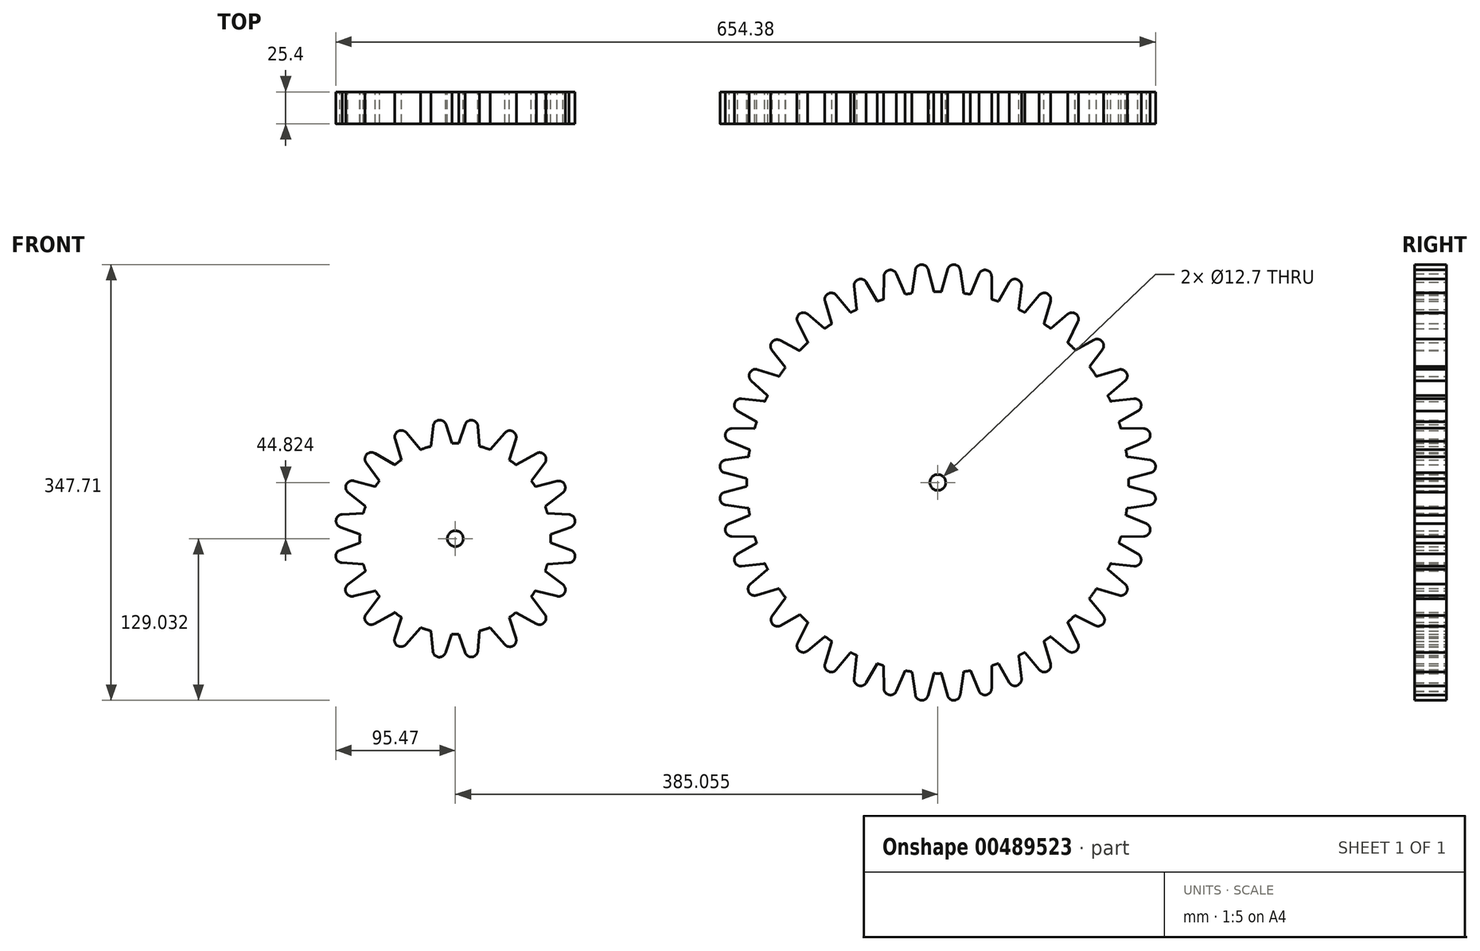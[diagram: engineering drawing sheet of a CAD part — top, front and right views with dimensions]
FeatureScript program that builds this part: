
annotation { "Feature Type Name" : "Feature", "Feature Type Description" : "" }
export const myFeature = defineFeature(function(context is Context, id is Id, definition is map)
    precondition{}
    {
        {
            var Q0;
            Q0=qCreatedBy(makeId("Front.planeOp"),FACE);
            var sketch = newSketch(context, id + "F0", { "sketchPlane" : qUnion([Q0])});
            skCircle(sketch, "E0", {"center": v(90.4, 32.98) * mm, "radius": 152.4 * mm});
            skCircle(sketch, "E1", {"center": v(90.4, 32.98) * mm, "radius": 6.35 * mm});
            skCircle(sketch, "E2", {"center": v(-294.65, -11.85) * mm, "radius": 76.2 * mm});
            skCircle(sketch, "E3", {"center": v(-294.65, -11.85) * mm, "radius": 6.35 * mm});
            skLineSegment(sketch, "E4", {"start": v(-78.98, 50.92) * mm, "end": v(-61.5, 53.51) * mm});
            skLineSegment(sketch, "E5", {"start": v(-57.15, 49.41) * mm, "end": v(-58.01, 39.52) * mm});
            skLineSegment(sketch, "E6", {"start": v(-62.8, 36.17) * mm, "end": v(-79.65, 40.7) * mm});
            skPoint(sketch, "E7.visualSharp", {"position": v(-82.74, 41.52) * mm});
            skPoint(sketch, "E8.visualSharp", {"position": v(-81.95, 50.47) * mm});
            skArc(sketch, "E9.filletArc", {"start": v(-57.15, 49.41) * mm, "mid": v(-58.33, 52.52) * mm, "end": v(-61.5, 53.51) * mm});
            skArc(sketch, "E10.filletArc", {"start": v(-62.8, 36.17) * mm, "mid": v(-59.62, 36.73) * mm, "end": v(-58.01, 39.52) * mm});
            skLineSegment(sketch, "E11", {"start": v(-66.15, 99.78) * mm, "end": v(-48.58, 97.84) * mm});
            skLineSegment(sketch, "E12", {"start": v(-45.42, 92.76) * mm, "end": v(-48.78, 83.42) * mm});
            skLineSegment(sketch, "E13", {"start": v(-54.25, 81.4) * mm, "end": v(-69.4, 90.07) * mm});
            skPoint(sketch, "E14.visualSharp", {"position": v(-72.18, 91.66) * mm});
            skArc(sketch, "E15.filletArc", {"start": v(-45.42, 92.76) * mm, "mid": v(-45.77, 96.07) * mm, "end": v(-48.58, 97.84) * mm});
            skArc(sketch, "E16.filletArc", {"start": v(-54.25, 81.4) * mm, "mid": v(-51.05, 81.13) * mm, "end": v(-48.78, 83.42) * mm});
            skLineSegment(sketch, "E17", {"start": v(-53.37, 123.14) * mm, "end": v(-37.03, 117.86) * mm});
            skLineSegment(sketch, "E18", {"start": v(-34.9, 112.33) * mm, "end": v(-39.88, 103.71) * mm});
            skLineSegment(sketch, "E19", {"start": v(-45.73, 102.79) * mm, "end": v(-58.48, 114.27) * mm});
            skPoint(sketch, "E20.visualSharp", {"position": v(-60.77, 116.34) * mm});
            skPoint(sketch, "E21.visualSharp", {"position": v(-56.3, 124.09) * mm});
            skArc(sketch, "E22.filletArc", {"start": v(-34.9, 112.33) * mm, "mid": v(-34.65, 115.6) * mm, "end": v(-37.03, 117.86) * mm});
            skArc(sketch, "E23.filletArc", {"start": v(-45.73, 102.79) * mm, "mid": v(-42.58, 101.85) * mm, "end": v(-39.88, 103.71) * mm});
            skLineSegment(sketch, "E24", {"start": v(-74.04, 75.96) * mm, "end": v(-56.37, 76.18) * mm});
            skLineSegment(sketch, "E25", {"start": v(-52.61, 71.53) * mm, "end": v(-54.8, 61.85) * mm});
            skLineSegment(sketch, "E26", {"start": v(-59.99, 59.17) * mm, "end": v(-76.08, 65.92) * mm});
            skPoint(sketch, "E27.visualSharp", {"position": v(-79.03, 67.15) * mm});
            skPoint(sketch, "E28.visualSharp", {"position": v(-77.05, 75.92) * mm});
            skArc(sketch, "E29.filletArc", {"start": v(-52.61, 71.53) * mm, "mid": v(-53.37, 74.77) * mm, "end": v(-56.37, 76.18) * mm});
            skArc(sketch, "E30.filletArc", {"start": v(-59.99, 59.17) * mm, "mid": v(-56.77, 59.3) * mm, "end": v(-54.8, 61.85) * mm});
            skLineSegment(sketch, "E31.MirrorCS", {"start": v(-7.67, 143.95) * mm, "end": v(-0.07, 150.34) * mm});
            skLineSegment(sketch, "E32.MirrorCS", {"start": v(-0.07, 156.17) * mm, "end": v(-13.44, 167.4) * mm});
            skLineSegment(sketch, "E33.MirrorCS", {"start": v(-21.43, 160.98) * mm, "end": v(-13.53, 145.17) * mm});
            skPoint(sketch, "E34.MirrorP", {"position": v(-22.77, 163.67) * mm});
            skArc(sketch, "E35.MirrorCS", {"start": v(-7.67, 143.95) * mm, "mid": v(-10.9, 143.14) * mm, "end": v(-13.53, 145.17) * mm});
            skArc(sketch, "E36.MirrorCS", {"start": v(-0.07, 156.17) * mm, "mid": v(1.3, 153.25) * mm, "end": v(-0.07, 150.34) * mm});
            skLineSegment(sketch, "E37.MirrorCS", {"start": v(10.98, 158.4) * mm, "end": v(19.58, 163.36) * mm});
            skArc(sketch, "E38.MirrorCS", {"start": v(10.98, 158.4) * mm, "mid": v(7.67, 158.16) * mm, "end": v(5.43, 160.61) * mm});
            skArc(sketch, "E39.MirrorCS", {"start": v(20.6, 169.11) * mm, "mid": v(21.43, 166) * mm, "end": v(19.58, 163.36) * mm});
            skLineSegment(sketch, "E40.MirrorCS", {"start": v(20.6, 169.11) * mm, "end": v(9.38, 182.48) * mm});
            skLineSegment(sketch, "E41.MirrorCS", {"start": v(0.4, 177.55) * mm, "end": v(5.43, 160.61) * mm});
            skPoint(sketch, "E42.MirrorP", {"position": v(-0.46, 180.43) * mm});
            skArc(sketch, "E43.MirrorCS", {"start": v(30.62, 168.8) * mm, "mid": v(27.32, 169.15) * mm, "end": v(25.55, 171.97) * mm});
            skLineSegment(sketch, "E44.MirrorCS", {"start": v(30.62, 168.8) * mm, "end": v(39.96, 172.16) * mm});
            skArc(sketch, "E45.MirrorCS", {"start": v(41.98, 177.64) * mm, "mid": v(42.25, 174.43) * mm, "end": v(39.96, 172.16) * mm});
            skLineSegment(sketch, "E46.MirrorCS", {"start": v(41.98, 177.64) * mm, "end": v(33.31, 192.78) * mm});
            skLineSegment(sketch, "E47.MirrorCS", {"start": v(23.6, 189.53) * mm, "end": v(25.55, 171.97) * mm});
            skLineSegment(sketch, "E48.MirrorCS", {"start": v(47.42, 197.43) * mm, "end": v(47.2, 179.76) * mm});
            skLineSegment(sketch, "E49.MirrorCS", {"start": v(64.2, 183.37) * mm, "end": v(57.47, 199.46) * mm});
            skArc(sketch, "E50.MirrorCS", {"start": v(64.2, 183.37) * mm, "mid": v(64.08, 180.15) * mm, "end": v(61.53, 178.18) * mm});
            skLineSegment(sketch, "E51.MirrorCS", {"start": v(51.85, 176) * mm, "end": v(61.53, 178.18) * mm});
            skArc(sketch, "E52.MirrorCS", {"start": v(51.85, 176) * mm, "mid": v(48.61, 176.75) * mm, "end": v(47.2, 179.76) * mm});
            skArc(sketch, "E53.MirrorCS", {"start": v(73.97, 180.53) * mm, "mid": v(70.86, 181.71) * mm, "end": v(69.87, 184.88) * mm});
            skLineSegment(sketch, "E54.MirrorCS", {"start": v(73.97, 180.53) * mm, "end": v(83.86, 181.4) * mm});
            skArc(sketch, "E55.MirrorCS", {"start": v(87.2, 186.17) * mm, "mid": v(86.65, 183) * mm, "end": v(83.86, 181.4) * mm});
            skLineSegment(sketch, "E56.MirrorCS", {"start": v(87.2, 186.17) * mm, "end": v(82.69, 203.03) * mm});
            skLineSegment(sketch, "E57.MirrorCS", {"start": v(72.47, 202.36) * mm, "end": v(69.87, 184.88) * mm});
            skLineSegment(sketch, "E58.MirrorCS", {"start": v(93.6, 186.17) * mm, "end": v(98.12, 203.03) * mm});
            skLineSegment(sketch, "E59.MirrorCS", {"start": v(108.35, 202.36) * mm, "end": v(110.94, 184.88) * mm});
            skArc(sketch, "E60.MirrorCS", {"start": v(106.84, 180.53) * mm, "mid": v(109.95, 181.71) * mm, "end": v(110.94, 184.88) * mm});
            skLineSegment(sketch, "E61.MirrorCS", {"start": v(106.84, 180.53) * mm, "end": v(96.95, 181.4) * mm});
            skArc(sketch, "E62.MirrorCS", {"start": v(93.6, 186.17) * mm, "mid": v(94.16, 183) * mm, "end": v(96.95, 181.4) * mm});
            skLineSegment(sketch, "E63.MirrorCS", {"start": v(133.39, 197.43) * mm, "end": v(133.6, 179.76) * mm});
            skArc(sketch, "E64.MirrorCS", {"start": v(128.96, 176) * mm, "mid": v(132.2, 176.75) * mm, "end": v(133.6, 179.76) * mm});
            skLineSegment(sketch, "E65.MirrorCS", {"start": v(128.96, 176) * mm, "end": v(119.28, 178.18) * mm});
            skArc(sketch, "E66.MirrorCS", {"start": v(116.6, 183.37) * mm, "mid": v(116.73, 180.15) * mm, "end": v(119.28, 178.18) * mm});
            skLineSegment(sketch, "E67.MirrorCS", {"start": v(116.6, 183.37) * mm, "end": v(123.35, 199.46) * mm});
            skLineSegment(sketch, "E68.MirrorCS", {"start": v(138.83, 177.64) * mm, "end": v(147.5, 192.78) * mm});
            skLineSegment(sketch, "E69.MirrorCS", {"start": v(157.21, 189.53) * mm, "end": v(155.27, 171.97) * mm});
            skArc(sketch, "E70.MirrorCS", {"start": v(150.2, 168.8) * mm, "mid": v(153.5, 169.15) * mm, "end": v(155.27, 171.97) * mm});
            skLineSegment(sketch, "E71.MirrorCS", {"start": v(150.2, 168.8) * mm, "end": v(140.85, 172.16) * mm});
            skArc(sketch, "E72.MirrorCS", {"start": v(138.83, 177.64) * mm, "mid": v(138.56, 174.43) * mm, "end": v(140.85, 172.16) * mm});
            skLineSegment(sketch, "E73.MirrorCS", {"start": v(160.22, 169.11) * mm, "end": v(171.43, 182.48) * mm});
            skLineSegment(sketch, "E74.MirrorCS", {"start": v(180.42, 177.55) * mm, "end": v(175.38, 160.61) * mm});
            skArc(sketch, "E75.MirrorCS", {"start": v(169.83, 158.4) * mm, "mid": v(173.14, 158.16) * mm, "end": v(175.38, 160.61) * mm});
            skLineSegment(sketch, "E76.MirrorCS", {"start": v(169.83, 158.4) * mm, "end": v(161.23, 163.36) * mm});
            skArc(sketch, "E77.MirrorCS", {"start": v(160.22, 169.11) * mm, "mid": v(159.38, 166) * mm, "end": v(161.23, 163.36) * mm});
            skArc(sketch, "E78.MirrorCS", {"start": v(180.88, 156.17) * mm, "mid": v(179.52, 153.25) * mm, "end": v(180.88, 150.34) * mm});
            skLineSegment(sketch, "E79.MirrorCS", {"start": v(180.88, 156.17) * mm, "end": v(194.25, 167.4) * mm});
            skLineSegment(sketch, "E80.MirrorCS", {"start": v(202.24, 160.98) * mm, "end": v(194.34, 145.17) * mm});
            skArc(sketch, "E81.MirrorCS", {"start": v(188.48, 143.95) * mm, "mid": v(191.7, 143.14) * mm, "end": v(194.34, 145.17) * mm});
            skLineSegment(sketch, "E82.MirrorCS", {"start": v(188.48, 143.95) * mm, "end": v(180.88, 150.34) * mm});
            skLineSegment(sketch, "E83.MirrorCS", {"start": v(234.98, 122.99) * mm, "end": v(218.04, 117.95) * mm});
            skLineSegment(sketch, "E84.MirrorCS", {"start": v(226.54, 102.79) * mm, "end": v(239.91, 114) * mm});
            skArc(sketch, "E85.MirrorCS", {"start": v(226.54, 102.79) * mm, "mid": v(223.43, 101.95) * mm, "end": v(220.8, 103.8) * mm});
            skArc(sketch, "E86.MirrorCS", {"start": v(215.83, 112.4) * mm, "mid": v(215.6, 115.71) * mm, "end": v(218.04, 117.95) * mm});
            skLineSegment(sketch, "E87.MirrorCS", {"start": v(246.96, 99.78) * mm, "end": v(229.4, 97.84) * mm});
            skPoint(sketch, "E88.MirrorP", {"position": v(252.99, 91.66) * mm});
            skLineSegment(sketch, "E89.MirrorCS", {"start": v(235.07, 81.4) * mm, "end": v(250.21, 90.07) * mm});
            skArc(sketch, "E90.MirrorCS", {"start": v(235.07, 81.4) * mm, "mid": v(231.86, 81.13) * mm, "end": v(229.59, 83.42) * mm});
            skLineSegment(sketch, "E91.MirrorCS", {"start": v(226.23, 92.76) * mm, "end": v(229.59, 83.42) * mm});
            skArc(sketch, "E92.MirrorCS", {"start": v(226.23, 92.76) * mm, "mid": v(226.58, 96.07) * mm, "end": v(229.4, 97.84) * mm});
            skArc(sketch, "E93.MirrorCS", {"start": v(233.42, 71.53) * mm, "mid": v(234.18, 74.77) * mm, "end": v(237.19, 76.18) * mm});
            skLineSegment(sketch, "E94.MirrorCS", {"start": v(254.86, 75.96) * mm, "end": v(237.19, 76.18) * mm});
            skLineSegment(sketch, "E95.MirrorCS", {"start": v(240.8, 59.17) * mm, "end": v(256.9, 65.92) * mm});
            skArc(sketch, "E96.MirrorCS", {"start": v(240.8, 59.17) * mm, "mid": v(237.58, 59.3) * mm, "end": v(235.6, 61.85) * mm});
            skLineSegment(sketch, "E97.MirrorCS", {"start": v(233.42, 71.53) * mm, "end": v(235.6, 61.85) * mm});
            skArc(sketch, "E98.MirrorCS", {"start": v(237.96, 49.41) * mm, "mid": v(239.14, 52.52) * mm, "end": v(242.31, 53.51) * mm});
            skLineSegment(sketch, "E99.MirrorCS", {"start": v(259.8, 50.92) * mm, "end": v(242.31, 53.51) * mm});
            skLineSegment(sketch, "E100.MirrorCS", {"start": v(243.6, 36.17) * mm, "end": v(260.46, 40.7) * mm});
            skArc(sketch, "E101.MirrorCS", {"start": v(243.6, 36.17) * mm, "mid": v(240.43, 36.73) * mm, "end": v(238.82, 39.52) * mm});
            skLineSegment(sketch, "E102.MirrorCS", {"start": v(237.96, 49.41) * mm, "end": v(238.82, 39.52) * mm});
            skArc(sketch, "E103.MirrorCS", {"start": v(-62.8, 29.78) * mm, "mid": v(-59.62, 29.22) * mm, "end": v(-58.01, 26.43) * mm});
            skLineSegment(sketch, "E104.MirrorCS", {"start": v(-57.15, 16.54) * mm, "end": v(-58.01, 26.43) * mm});
            skArc(sketch, "E105.MirrorCS", {"start": v(-57.15, 16.54) * mm, "mid": v(-58.33, 13.43) * mm, "end": v(-61.5, 12.44) * mm});
            skLineSegment(sketch, "E106.MirrorCS", {"start": v(-78.98, 15.04) * mm, "end": v(-61.5, 12.44) * mm});
            skPoint(sketch, "E107.MirrorP", {"position": v(-81.95, 15.48) * mm});
            skPoint(sketch, "E108.MirrorP", {"position": v(-82.74, 24.43) * mm});
            skLineSegment(sketch, "E109.MirrorCS", {"start": v(-62.8, 29.78) * mm, "end": v(-79.65, 25.26) * mm});
            skLineSegment(sketch, "E110.MirrorCS", {"start": v(-59.99, 6.78) * mm, "end": v(-76.08, 0.04) * mm});
            skPoint(sketch, "E111.MirrorP", {"position": v(-79.03, -1.2) * mm});
            skLineSegment(sketch, "E112.MirrorCS", {"start": v(-74.04, -10) * mm, "end": v(-56.37, -10.23) * mm});
            skArc(sketch, "E113.MirrorCS", {"start": v(-52.61, -5.58) * mm, "mid": v(-53.37, -8.82) * mm, "end": v(-56.37, -10.23) * mm});
            skLineSegment(sketch, "E114.MirrorCS", {"start": v(-52.61, -5.58) * mm, "end": v(-54.8, 4.1) * mm});
            skArc(sketch, "E115.MirrorCS", {"start": v(-59.99, 6.78) * mm, "mid": v(-56.77, 6.65) * mm, "end": v(-54.8, 4.1) * mm});
            skArc(sketch, "E116.MirrorCS", {"start": v(-54.25, -15.45) * mm, "mid": v(-51.05, -15.18) * mm, "end": v(-48.78, -17.47) * mm});
            skLineSegment(sketch, "E117.MirrorCS", {"start": v(-45.42, -26.8) * mm, "end": v(-48.78, -17.47) * mm});
            skArc(sketch, "E118.MirrorCS", {"start": v(-45.42, -26.8) * mm, "mid": v(-45.77, -30.11) * mm, "end": v(-48.58, -31.88) * mm});
            skLineSegment(sketch, "E119.MirrorCS", {"start": v(-66.15, -33.83) * mm, "end": v(-48.58, -31.88) * mm});
            skPoint(sketch, "E120.MirrorP", {"position": v(-69.14, -34.16) * mm});
            skPoint(sketch, "E121.MirrorP", {"position": v(-72.18, -25.7) * mm});
            skLineSegment(sketch, "E122.MirrorCS", {"start": v(-54.25, -15.45) * mm, "end": v(-69.4, -24.12) * mm});
            skArc(sketch, "E123.MirrorCS", {"start": v(-45.73, -36.84) * mm, "mid": v(-42.62, -36) * mm, "end": v(-39.98, -37.85) * mm});
            skArc(sketch, "E124.MirrorCS", {"start": v(-35.02, -46.45) * mm, "mid": v(-34.78, -49.76) * mm, "end": v(-37.23, -52) * mm});
            skLineSegment(sketch, "E125.MirrorCS", {"start": v(-54.17, -57.04) * mm, "end": v(-37.23, -52) * mm});
            skLineSegment(sketch, "E126.MirrorCS", {"start": v(-45.73, -36.84) * mm, "end": v(-59.1, -48.05) * mm});
            skArc(sketch, "E127.MirrorCS", {"start": v(-7.67, -78) * mm, "mid": v(-10.9, -77.2) * mm, "end": v(-13.53, -79.22) * mm});
            skLineSegment(sketch, "E128.MirrorCS", {"start": v(-7.67, -78) * mm, "end": v(-0.07, -84.38) * mm});
            skArc(sketch, "E129.MirrorCS", {"start": v(-0.07, -90.22) * mm, "mid": v(1.3, -87.3) * mm, "end": v(-0.07, -84.38) * mm});
            skLineSegment(sketch, "E130.MirrorCS", {"start": v(-0.07, -90.22) * mm, "end": v(-13.44, -101.44) * mm});
            skLineSegment(sketch, "E131.MirrorCS", {"start": v(-35.02, -46.45) * mm, "end": v(-39.98, -37.85) * mm});
            skLineSegment(sketch, "E132.MirrorCS", {"start": v(-21.43, -95.03) * mm, "end": v(-13.53, -79.22) * mm});
            skArc(sketch, "E133.MirrorCS", {"start": v(10.98, -92.45) * mm, "mid": v(7.67, -92.2) * mm, "end": v(5.43, -94.66) * mm});
            skLineSegment(sketch, "E134.MirrorCS", {"start": v(0.4, -111.6) * mm, "end": v(5.43, -94.66) * mm});
            skLineSegment(sketch, "E135.MirrorCS", {"start": v(20.6, -103.16) * mm, "end": v(9.38, -116.53) * mm});
            skArc(sketch, "E136.MirrorCS", {"start": v(20.6, -103.16) * mm, "mid": v(21.43, -100.05) * mm, "end": v(19.58, -97.41) * mm});
            skLineSegment(sketch, "E137.MirrorCS", {"start": v(10.98, -92.45) * mm, "end": v(19.58, -97.41) * mm});
            skArc(sketch, "E138.MirrorCS", {"start": v(30.62, -102.85) * mm, "mid": v(27.32, -103.2) * mm, "end": v(25.55, -106.01) * mm});
            skLineSegment(sketch, "E139.MirrorCS", {"start": v(30.62, -102.85) * mm, "end": v(39.96, -106.2) * mm});
            skArc(sketch, "E140.MirrorCS", {"start": v(41.98, -111.68) * mm, "mid": v(42.25, -108.48) * mm, "end": v(39.96, -106.2) * mm});
            skLineSegment(sketch, "E141.MirrorCS", {"start": v(41.98, -111.68) * mm, "end": v(33.31, -126.83) * mm});
            skArc(sketch, "E142.MirrorCS", {"start": v(28.72, -128.53) * mm, "mid": v(31.32, -128.52) * mm, "end": v(33.31, -126.83) * mm});
            skLineSegment(sketch, "E143.MirrorCS", {"start": v(23.6, -123.58) * mm, "end": v(25.55, -106.01) * mm});
            skLineSegment(sketch, "E144.MirrorCS", {"start": v(47.42, -131.47) * mm, "end": v(47.2, -113.8) * mm});
            skArc(sketch, "E145.MirrorCS", {"start": v(51.85, -110.04) * mm, "mid": v(48.61, -110.8) * mm, "end": v(47.2, -113.8) * mm});
            skLineSegment(sketch, "E146.MirrorCS", {"start": v(51.85, -110.04) * mm, "end": v(61.53, -112.23) * mm});
            skArc(sketch, "E147.MirrorCS", {"start": v(64.2, -117.42) * mm, "mid": v(64.08, -114.2) * mm, "end": v(61.53, -112.23) * mm});
            skLineSegment(sketch, "E148.MirrorCS", {"start": v(64.2, -117.42) * mm, "end": v(57.47, -133.51) * mm});
            skLineSegment(sketch, "E149.MirrorCS", {"start": v(72.47, -136.41) * mm, "end": v(69.87, -118.93) * mm});
            skArc(sketch, "E150.MirrorCS", {"start": v(73.97, -114.58) * mm, "mid": v(70.86, -115.76) * mm, "end": v(69.87, -118.93) * mm});
            skLineSegment(sketch, "E151.MirrorCS", {"start": v(73.97, -114.58) * mm, "end": v(83.86, -115.44) * mm});
            skArc(sketch, "E152.MirrorCS", {"start": v(87.2, -120.22) * mm, "mid": v(86.65, -117.05) * mm, "end": v(83.86, -115.44) * mm});
            skLineSegment(sketch, "E153.MirrorCS", {"start": v(87.2, -120.22) * mm, "end": v(82.69, -137.08) * mm});
            skLineSegment(sketch, "E154.MirrorCS", {"start": v(93.6, -120.22) * mm, "end": v(98.12, -137.08) * mm});
            skArc(sketch, "E155.MirrorCS", {"start": v(93.6, -120.22) * mm, "mid": v(94.16, -117.05) * mm, "end": v(96.95, -115.44) * mm});
            skLineSegment(sketch, "E156.MirrorCS", {"start": v(106.84, -114.58) * mm, "end": v(96.95, -115.44) * mm});
            skArc(sketch, "E157.MirrorCS", {"start": v(106.84, -114.58) * mm, "mid": v(109.95, -115.76) * mm, "end": v(110.94, -118.93) * mm});
            skLineSegment(sketch, "E158.MirrorCS", {"start": v(108.35, -136.41) * mm, "end": v(110.94, -118.93) * mm});
            skArc(sketch, "E159.MirrorCS", {"start": v(127.7, -135.76) * mm, "mid": v(125.11, -135.43) * mm, "end": v(123.35, -133.51) * mm});
            skLineSegment(sketch, "E160.MirrorCS", {"start": v(133.39, -131.47) * mm, "end": v(133.6, -113.8) * mm});
            skArc(sketch, "E161.MirrorCS", {"start": v(128.96, -110.04) * mm, "mid": v(132.2, -110.8) * mm, "end": v(133.6, -113.8) * mm});
            skLineSegment(sketch, "E162.MirrorCS", {"start": v(128.96, -110.04) * mm, "end": v(119.28, -112.23) * mm});
            skArc(sketch, "E163.MirrorCS", {"start": v(116.6, -117.42) * mm, "mid": v(116.73, -114.2) * mm, "end": v(119.28, -112.23) * mm});
            skLineSegment(sketch, "E164.MirrorCS", {"start": v(116.6, -117.42) * mm, "end": v(123.35, -133.51) * mm});
            skLineSegment(sketch, "E165.MirrorCS", {"start": v(152.1, -128.53) * mm, "end": v(154.72, -127.58) * mm});
            skArc(sketch, "E166.MirrorCS", {"start": v(150.2, -102.85) * mm, "mid": v(153.5, -103.2) * mm, "end": v(155.27, -106.01) * mm});
            skArc(sketch, "E167.MirrorCS", {"start": v(138.83, -111.68) * mm, "mid": v(138.56, -108.48) * mm, "end": v(140.85, -106.2) * mm});
            skLineSegment(sketch, "E168.MirrorCS", {"start": v(138.83, -111.68) * mm, "end": v(147.5, -126.83) * mm});
            skLineSegment(sketch, "E169.MirrorCS", {"start": v(160.22, -103.16) * mm, "end": v(171.43, -116.53) * mm});
            skLineSegment(sketch, "E170.MirrorCS", {"start": v(180.42, -111.6) * mm, "end": v(175.38, -94.66) * mm});
            skArc(sketch, "E171.MirrorCS", {"start": v(169.83, -92.45) * mm, "mid": v(173.14, -92.2) * mm, "end": v(175.38, -94.66) * mm});
            skArc(sketch, "E172.MirrorCS", {"start": v(160.22, -103.16) * mm, "mid": v(159.38, -100.05) * mm, "end": v(161.23, -97.41) * mm});
            skLineSegment(sketch, "E173.MirrorCS", {"start": v(180.88, -90.22) * mm, "end": v(194.25, -101.44) * mm});
            skArc(sketch, "E174.MirrorCS", {"start": v(180.88, -90.22) * mm, "mid": v(179.52, -87.3) * mm, "end": v(180.88, -84.38) * mm});
            skLineSegment(sketch, "E175.MirrorCS", {"start": v(188.48, -78) * mm, "end": v(180.88, -84.38) * mm});
            skArc(sketch, "E176.MirrorCS", {"start": v(188.48, -78) * mm, "mid": v(191.7, -77.2) * mm, "end": v(194.34, -79.22) * mm});
            skLineSegment(sketch, "E177.MirrorCS", {"start": v(202.24, -95.03) * mm, "end": v(194.34, -79.22) * mm});
            skLineSegment(sketch, "E178.MirrorCS", {"start": v(234.98, -57.04) * mm, "end": v(218.04, -52) * mm});
            skLineSegment(sketch, "E179.MirrorCS", {"start": v(226.54, -36.84) * mm, "end": v(239.91, -48.05) * mm});
            skArc(sketch, "E180.MirrorCS", {"start": v(226.54, -36.84) * mm, "mid": v(223.43, -36) * mm, "end": v(220.8, -37.85) * mm});
            skLineSegment(sketch, "E181.MirrorCS", {"start": v(215.83, -46.45) * mm, "end": v(220.8, -37.85) * mm});
            skArc(sketch, "E182.MirrorCS", {"start": v(215.83, -46.45) * mm, "mid": v(215.6, -49.76) * mm, "end": v(218.04, -52) * mm});
            skLineSegment(sketch, "E183.MirrorCS", {"start": v(246.96, -33.83) * mm, "end": v(229.4, -31.88) * mm});
            skArc(sketch, "E184.MirrorCS", {"start": v(226.23, -26.8) * mm, "mid": v(226.58, -30.11) * mm, "end": v(229.4, -31.88) * mm});
            skLineSegment(sketch, "E185.MirrorCS", {"start": v(226.23, -26.8) * mm, "end": v(229.59, -17.47) * mm});
            skArc(sketch, "E186.MirrorCS", {"start": v(235.07, -15.45) * mm, "mid": v(231.86, -15.18) * mm, "end": v(229.59, -17.47) * mm});
            skLineSegment(sketch, "E187.MirrorCS", {"start": v(235.07, -15.45) * mm, "end": v(250.21, -24.12) * mm});
            skPoint(sketch, "E188.MirrorP", {"position": v(249.95, -34.16) * mm});
            skLineSegment(sketch, "E189.MirrorCS", {"start": v(254.86, -10) * mm, "end": v(237.19, -10.23) * mm});
            skArc(sketch, "E190.MirrorCS", {"start": v(233.42, -5.58) * mm, "mid": v(234.18, -8.82) * mm, "end": v(237.19, -10.23) * mm});
            skLineSegment(sketch, "E191.MirrorCS", {"start": v(240.8, 6.78) * mm, "end": v(256.9, 0.04) * mm});
            skLineSegment(sketch, "E192.MirrorCS", {"start": v(259.8, 15.04) * mm, "end": v(242.31, 12.44) * mm});
            skLineSegment(sketch, "E193.MirrorCS", {"start": v(237.96, 16.54) * mm, "end": v(238.82, 26.43) * mm});
            skArc(sketch, "E194.MirrorCS", {"start": v(243.6, 29.78) * mm, "mid": v(240.43, 29.22) * mm, "end": v(238.82, 26.43) * mm});
            skLineSegment(sketch, "E195.MirrorCS", {"start": v(243.6, 29.78) * mm, "end": v(260.46, 25.26) * mm});
            skLineSegment(sketch, "E196.MirrorCS", {"start": v(150.2, -102.85) * mm, "end": v(140.85, -106.2) * mm});
            skLineSegment(sketch, "E197.MirrorCS", {"start": v(169.83, -92.45) * mm, "end": v(161.23, -97.41) * mm});
            skLineSegment(sketch, "E198.MirrorCS", {"start": v(157.21, -123.58) * mm, "end": v(155.27, -106.01) * mm});
            skArc(sketch, "E199.MirrorCS", {"start": v(237.96, 16.54) * mm, "mid": v(239.14, 13.43) * mm, "end": v(242.31, 12.44) * mm});
            skLineSegment(sketch, "E200.MirrorCS", {"start": v(233.42, -5.58) * mm, "end": v(235.6, 4.1) * mm});
            skArc(sketch, "E201.MirrorCS", {"start": v(240.8, 6.78) * mm, "mid": v(237.58, 6.65) * mm, "end": v(235.6, 4.1) * mm});
            skLineSegment(sketch, "E202", {"start": v(-384.91, 7.54) * mm, "end": v(-367.48, 8.47) * mm});
            skLineSegment(sketch, "E203", {"start": v(-363.53, 4) * mm, "end": v(-365.25, -5.78) * mm});
            skLineSegment(sketch, "E204", {"start": v(-370.35, -8.69) * mm, "end": v(-386.54, -2.57) * mm});
            skPoint(sketch, "E205.visualSharp", {"position": v(-389.5, -1.46) * mm});
            skPoint(sketch, "E206.visualSharp", {"position": v(-387.93, 7.38) * mm});
            skArc(sketch, "E207.filletArc", {"start": v(-363.53, 4) * mm, "mid": v(-364.43, 7.19) * mm, "end": v(-367.48, 8.47) * mm});
            skArc(sketch, "E208.filletArc", {"start": v(-370.35, -8.69) * mm, "mid": v(-367.12, -8.43) * mm, "end": v(-365.25, -5.78) * mm});
            skLineSegment(sketch, "E209", {"start": v(-302.17, 79.14) * mm, "end": v(-296.85, 62.3) * mm});
            skLineSegment(sketch, "E210", {"start": v(-300.15, 57.37) * mm, "end": v(-310.03, 56.5) * mm});
            skLineSegment(sketch, "E211", {"start": v(-314.15, 60.68) * mm, "end": v(-312.37, 78.14) * mm});
            skPoint(sketch, "E212.visualSharp", {"position": v(-312.05, 81.27) * mm});
            skPoint(sketch, "E213.visualSharp", {"position": v(-303.09, 82.05) * mm});
            skArc(sketch, "E214.filletArc", {"start": v(-300.15, 57.37) * mm, "mid": v(-297.31, 59.04) * mm, "end": v(-296.85, 62.3) * mm});
            skArc(sketch, "E215.filletArc", {"start": v(-314.15, 60.68) * mm, "mid": v(-313.07, 57.62) * mm, "end": v(-310.03, 56.5) * mm});
            skLineSegment(sketch, "E216", {"start": v(-358.91, 56.25) * mm, "end": v(-343.72, 47.43) * mm});
            skLineSegment(sketch, "E217", {"start": v(-342.84, 41.55) * mm, "end": v(-349.59, 34.25) * mm});
            skLineSegment(sketch, "E218", {"start": v(-355.45, 34.58) * mm, "end": v(-365.8, 48.66) * mm});
            skPoint(sketch, "E219.visualSharp", {"position": v(-367.65, 51.2) * mm});
            skPoint(sketch, "E220.visualSharp", {"position": v(-361.55, 57.78) * mm});
            skArc(sketch, "E221.filletArc", {"start": v(-342.84, 41.55) * mm, "mid": v(-341.86, 44.7) * mm, "end": v(-343.72, 47.43) * mm});
            skArc(sketch, "E222.filletArc", {"start": v(-355.45, 34.58) * mm, "mid": v(-352.6, 33.04) * mm, "end": v(-349.59, 34.25) * mm});
            skLineSegment(sketch, "E223", {"start": v(-333.8, 72.69) * mm, "end": v(-322.4, 59.2) * mm});
            skLineSegment(sketch, "E224", {"start": v(-323.54, 53.36) * mm, "end": v(-332.34, 48.75) * mm});
            skLineSegment(sketch, "E225", {"start": v(-337.76, 51.02) * mm, "end": v(-342.82, 67.84) * mm});
            skPoint(sketch, "E226.visualSharp", {"position": v(-343.73, 70.85) * mm});
            skPoint(sketch, "E227.visualSharp", {"position": v(-335.77, 75.02) * mm});
            skArc(sketch, "E228.filletArc", {"start": v(-323.54, 53.36) * mm, "mid": v(-321.57, 56) * mm, "end": v(-322.4, 59.2) * mm});
            skArc(sketch, "E229.filletArc", {"start": v(-337.76, 51.02) * mm, "mid": v(-335.58, 48.6) * mm, "end": v(-332.34, 48.75) * mm});
            skLineSegment(sketch, "E230", {"start": v(-375.59, 34.19) * mm, "end": v(-358.66, 29.72) * mm});
            skLineSegment(sketch, "E231", {"start": v(-356.25, 24.27) * mm, "end": v(-360.85, 15.46) * mm});
            skLineSegment(sketch, "E232", {"start": v(-366.6, 14.24) * mm, "end": v(-380.22, 25.05) * mm});
            skPoint(sketch, "E233.visualSharp", {"position": v(-382.69, 27) * mm});
            skPoint(sketch, "E234.visualSharp", {"position": v(-378.53, 34.96) * mm});
            skArc(sketch, "E235.filletArc", {"start": v(-356.25, 24.27) * mm, "mid": v(-356.14, 27.57) * mm, "end": v(-358.66, 29.72) * mm});
            skArc(sketch, "E236.filletArc", {"start": v(-366.6, 14.24) * mm, "mid": v(-363.44, 13.5) * mm, "end": v(-360.85, 15.46) * mm});
            skLineSegment(sketch, "E237.MirrorCS", {"start": v(-286.86, 79.07) * mm, "end": v(-292.45, 62.3) * mm});
            skArc(sketch, "E238.MirrorCS", {"start": v(-289.17, 57.3) * mm, "mid": v(-292.02, 59.01) * mm, "end": v(-292.45, 62.3) * mm});
            skLineSegment(sketch, "E239.MirrorCS", {"start": v(-289.17, 57.3) * mm, "end": v(-279.28, 56.44) * mm});
            skArc(sketch, "E240.MirrorCS", {"start": v(-275.15, 60.57) * mm, "mid": v(-276.25, 57.54) * mm, "end": v(-279.28, 56.44) * mm});
            skLineSegment(sketch, "E241.MirrorCS", {"start": v(-275.15, 60.57) * mm, "end": v(-276.67, 77.95) * mm});
            skPoint(sketch, "E242.MirrorP", {"position": v(-276.95, 81.14) * mm});
            skLineSegment(sketch, "E243.MirrorCS", {"start": v(-251.54, 51.02) * mm, "end": v(-246.24, 67.65) * mm});
            skLineSegment(sketch, "E244.MirrorCS", {"start": v(-265.73, 53.42) * mm, "end": v(-256.94, 48.8) * mm});
            skArc(sketch, "E245.MirrorCS", {"start": v(-265.73, 53.42) * mm, "mid": v(-267.7, 56.09) * mm, "end": v(-266.83, 59.3) * mm});
            skLineSegment(sketch, "E246.MirrorCS", {"start": v(-255.21, 72.6) * mm, "end": v(-266.83, 59.3) * mm});
            skLineSegment(sketch, "E247.MirrorCS", {"start": v(-230.08, 56.15) * mm, "end": v(-245.49, 47.5) * mm});
            skArc(sketch, "E248.MirrorCS", {"start": v(-251.54, 51.02) * mm, "mid": v(-253.73, 48.65) * mm, "end": v(-256.94, 48.8) * mm});
            skLineSegment(sketch, "E249.MirrorCS", {"start": v(-233.85, 34.58) * mm, "end": v(-223.3, 48.48) * mm});
            skArc(sketch, "E250.MirrorCS", {"start": v(-233.85, 34.58) * mm, "mid": v(-236.7, 33.08) * mm, "end": v(-239.68, 34.3) * mm});
            skLineSegment(sketch, "E251.MirrorCS", {"start": v(-246.42, 41.59) * mm, "end": v(-239.68, 34.3) * mm});
            skArc(sketch, "E252.MirrorCS", {"start": v(-246.42, 41.59) * mm, "mid": v(-247.39, 44.77) * mm, "end": v(-245.49, 47.5) * mm});
            skLineSegment(sketch, "E253.MirrorCS", {"start": v(-213.41, 34.07) * mm, "end": v(-230.55, 29.76) * mm});
            skArc(sketch, "E254.MirrorCS", {"start": v(-233, 24.3) * mm, "mid": v(-233.1, 27.62) * mm, "end": v(-230.55, 29.76) * mm});
            skLineSegment(sketch, "E255.MirrorCS", {"start": v(-233, 24.3) * mm, "end": v(-228.4, 15.5) * mm});
            skArc(sketch, "E256.MirrorCS", {"start": v(-222.7, 14.24) * mm, "mid": v(-225.84, 13.54) * mm, "end": v(-228.4, 15.5) * mm});
            skLineSegment(sketch, "E257.MirrorCS", {"start": v(-222.7, 14.24) * mm, "end": v(-208.87, 24.89) * mm});
            skLineSegment(sketch, "E258.MirrorCS", {"start": v(-204.1, 7.41) * mm, "end": v(-221.75, 8.47) * mm});
            skArc(sketch, "E259.MirrorCS", {"start": v(-225.73, 4) * mm, "mid": v(-224.82, 7.2) * mm, "end": v(-221.75, 8.47) * mm});
            skLineSegment(sketch, "E260.MirrorCS", {"start": v(-225.73, 4) * mm, "end": v(-224, -5.77) * mm});
            skArc(sketch, "E261.MirrorCS", {"start": v(-218.95, -8.69) * mm, "mid": v(-222.16, -8.4) * mm, "end": v(-224, -5.77) * mm});
            skLineSegment(sketch, "E262.MirrorCS", {"start": v(-218.95, -8.69) * mm, "end": v(-202.55, -2.72) * mm});
            skLineSegment(sketch, "E263.MirrorCS", {"start": v(-370.35, -15.01) * mm, "end": v(-386.75, -20.98) * mm});
            skArc(sketch, "E264.MirrorCS", {"start": v(-370.35, -15.01) * mm, "mid": v(-367.14, -15.3) * mm, "end": v(-365.3, -17.93) * mm});
            skLineSegment(sketch, "E265.MirrorCS", {"start": v(-363.57, -27.7) * mm, "end": v(-365.3, -17.93) * mm});
            skArc(sketch, "E266.MirrorCS", {"start": v(-363.57, -27.7) * mm, "mid": v(-364.48, -30.9) * mm, "end": v(-367.55, -32.17) * mm});
            skLineSegment(sketch, "E267.MirrorCS", {"start": v(-385.2, -31.1) * mm, "end": v(-367.55, -32.17) * mm});
            skLineSegment(sketch, "E268.MirrorCS", {"start": v(-366.6, -37.94) * mm, "end": v(-380.43, -48.58) * mm});
            skArc(sketch, "E269.MirrorCS", {"start": v(-366.6, -37.94) * mm, "mid": v(-363.46, -37.24) * mm, "end": v(-360.9, -39.2) * mm});
            skLineSegment(sketch, "E270.MirrorCS", {"start": v(-356.3, -48) * mm, "end": v(-360.9, -39.2) * mm});
            skArc(sketch, "E271.MirrorCS", {"start": v(-356.3, -48) * mm, "mid": v(-356.2, -51.32) * mm, "end": v(-358.75, -53.45) * mm});
            skLineSegment(sketch, "E272.MirrorCS", {"start": v(-375.89, -57.77) * mm, "end": v(-358.75, -53.45) * mm});
            skArc(sketch, "E273.MirrorCS", {"start": v(-355.45, -58.28) * mm, "mid": v(-352.6, -56.78) * mm, "end": v(-349.62, -58) * mm});
            skLineSegment(sketch, "E274.MirrorCS", {"start": v(-355.45, -58.28) * mm, "end": v(-366, -72.18) * mm});
            skLineSegment(sketch, "E275.MirrorCS", {"start": v(-359.22, -79.85) * mm, "end": v(-343.81, -71.2) * mm});
            skArc(sketch, "E276.MirrorCS", {"start": v(-342.88, -65.28) * mm, "mid": v(-341.91, -68.46) * mm, "end": v(-343.81, -71.2) * mm});
            skLineSegment(sketch, "E277.MirrorCS", {"start": v(-342.88, -65.28) * mm, "end": v(-349.62, -58) * mm});
            skArc(sketch, "E278.MirrorCS", {"start": v(-337.76, -74.72) * mm, "mid": v(-335.57, -72.35) * mm, "end": v(-332.36, -72.5) * mm});
            skLineSegment(sketch, "E279.MirrorCS", {"start": v(-337.76, -74.72) * mm, "end": v(-343.06, -91.35) * mm});
            skLineSegment(sketch, "E280.MirrorCS", {"start": v(-334.09, -96.3) * mm, "end": v(-322.47, -83) * mm});
            skArc(sketch, "E281.MirrorCS", {"start": v(-323.57, -77.11) * mm, "mid": v(-321.6, -79.79) * mm, "end": v(-322.47, -83) * mm});
            skLineSegment(sketch, "E282.MirrorCS", {"start": v(-323.57, -77.11) * mm, "end": v(-332.36, -72.5) * mm});
            skArc(sketch, "E283.MirrorCS", {"start": v(-314.15, -84.27) * mm, "mid": v(-313.05, -81.24) * mm, "end": v(-310.02, -80.14) * mm});
            skLineSegment(sketch, "E284.MirrorCS", {"start": v(-300.13, -81) * mm, "end": v(-310.02, -80.14) * mm});
            skArc(sketch, "E285.MirrorCS", {"start": v(-300.13, -81) * mm, "mid": v(-297.28, -82.7) * mm, "end": v(-296.85, -86) * mm});
            skLineSegment(sketch, "E286.MirrorCS", {"start": v(-302.44, -102.77) * mm, "end": v(-296.85, -86) * mm});
            skPoint(sketch, "E287.MirrorP", {"position": v(-303.4, -105.62) * mm});
            skLineSegment(sketch, "E288.MirrorCS", {"start": v(-314.15, -84.27) * mm, "end": v(-312.63, -101.65) * mm});
            skArc(sketch, "E289.MirrorCS", {"start": v(-289.17, -81) * mm, "mid": v(-292.02, -82.7) * mm, "end": v(-292.45, -86) * mm});
            skLineSegment(sketch, "E290.MirrorCS", {"start": v(-289.17, -81) * mm, "end": v(-279.28, -80.14) * mm});
            skArc(sketch, "E291.MirrorCS", {"start": v(-275.15, -84.27) * mm, "mid": v(-276.25, -81.24) * mm, "end": v(-279.28, -80.14) * mm});
            skLineSegment(sketch, "E292.MirrorCS", {"start": v(-275.15, -84.27) * mm, "end": v(-276.67, -101.65) * mm});
            skLineSegment(sketch, "E293.MirrorCS", {"start": v(-286.86, -102.77) * mm, "end": v(-292.45, -86) * mm});
            skArc(sketch, "E294.MirrorCS", {"start": v(-265.73, -77.11) * mm, "mid": v(-267.7, -79.79) * mm, "end": v(-266.83, -83) * mm});
            skLineSegment(sketch, "E295.MirrorCS", {"start": v(-265.73, -77.11) * mm, "end": v(-256.94, -72.5) * mm});
            skArc(sketch, "E296.MirrorCS", {"start": v(-251.54, -74.72) * mm, "mid": v(-253.73, -72.35) * mm, "end": v(-256.94, -72.5) * mm});
            skLineSegment(sketch, "E297.MirrorCS", {"start": v(-255.21, -96.3) * mm, "end": v(-266.83, -83) * mm});
            skLineSegment(sketch, "E298.MirrorCS", {"start": v(-246.42, -65.28) * mm, "end": v(-239.68, -58) * mm});
            skArc(sketch, "E299.MirrorCS", {"start": v(-246.42, -65.28) * mm, "mid": v(-247.39, -68.46) * mm, "end": v(-245.49, -71.2) * mm});
            skLineSegment(sketch, "E300.MirrorCS", {"start": v(-233.85, -58.28) * mm, "end": v(-223.3, -72.18) * mm});
            skArc(sketch, "E301.MirrorCS", {"start": v(-233, -48) * mm, "mid": v(-233.1, -51.32) * mm, "end": v(-230.55, -53.45) * mm});
            skLineSegment(sketch, "E302.MirrorCS", {"start": v(-233, -48) * mm, "end": v(-228.4, -39.2) * mm});
            skArc(sketch, "E303.MirrorCS", {"start": v(-222.7, -37.94) * mm, "mid": v(-225.84, -37.24) * mm, "end": v(-228.4, -39.2) * mm});
            skLineSegment(sketch, "E304.MirrorCS", {"start": v(-222.7, -37.94) * mm, "end": v(-208.87, -48.58) * mm});
            skLineSegment(sketch, "E305.MirrorCS", {"start": v(-213.41, -57.77) * mm, "end": v(-230.55, -53.45) * mm});
            skLineSegment(sketch, "E306.MirrorCS", {"start": v(-204.1, -31.1) * mm, "end": v(-221.75, -32.17) * mm});
            skArc(sketch, "E307.MirrorCS", {"start": v(-225.73, -27.7) * mm, "mid": v(-224.82, -30.9) * mm, "end": v(-221.75, -32.17) * mm});
            skLineSegment(sketch, "E308.MirrorCS", {"start": v(-225.73, -27.7) * mm, "end": v(-224, -17.93) * mm});
            skArc(sketch, "E309.MirrorCS", {"start": v(-218.95, -15.01) * mm, "mid": v(-222.16, -15.3) * mm, "end": v(-224, -17.93) * mm});
            skLineSegment(sketch, "E310.MirrorCS", {"start": v(-218.95, -15.01) * mm, "end": v(-202.55, -20.98) * mm});
            skLineSegment(sketch, "E311.MirrorCS", {"start": v(-251.54, -74.72) * mm, "end": v(-246.24, -91.35) * mm});
            skArc(sketch, "E312.MirrorCS", {"start": v(-233.85, -58.28) * mm, "mid": v(-236.7, -56.78) * mm, "end": v(-239.68, -58) * mm});
            skLineSegment(sketch, "E313.MirrorCS", {"start": v(-230.08, -79.85) * mm, "end": v(-245.49, -71.2) * mm});
            skLineSegment(sketch, "E314", {"start": v(221.78, 139.03) * mm, "end": v(211.23, 125.2) * mm});
            skLineSegment(sketch, "E315", {"start": v(205.28, 125.06) * mm, "end": v(198.9, 132.65) * mm});
            skLineSegment(sketch, "E316", {"start": v(199.98, 138.43) * mm, "end": v(215.11, 146.8) * mm});
            skPoint(sketch, "E317.visualSharp", {"position": v(217.86, 148.33) * mm});
            skPoint(sketch, "E318.visualSharp", {"position": v(223.62, 141.45) * mm});
            skArc(sketch, "E319.filletArc", {"start": v(205.28, 125.06) * mm, "mid": v(208.29, 123.7) * mm, "end": v(211.23, 125.2) * mm});
            skArc(sketch, "E320.filletArc", {"start": v(199.98, 138.43) * mm, "mid": v(198.08, 135.8) * mm, "end": v(198.9, 132.65) * mm});
            skLineSegment(sketch, "E321", {"start": v(-35.33, 146.4) * mm, "end": v(-20.14, 138.22) * mm});
            skLineSegment(sketch, "E322", {"start": v(-19.02, 132.42) * mm, "end": v(-25.42, 124.8) * mm});
            skLineSegment(sketch, "E323", {"start": v(-31.35, 124.9) * mm, "end": v(-41.94, 138.57) * mm});
            skPoint(sketch, "E324.visualSharp", {"position": v(-43.82, 141) * mm});
            skPoint(sketch, "E325.visualSharp", {"position": v(-38.06, 147.86) * mm});
            skArc(sketch, "E326.filletArc", {"start": v(-19.02, 132.42) * mm, "mid": v(-18.2, 135.59) * mm, "end": v(-20.14, 138.22) * mm});
            skArc(sketch, "E327.filletArc", {"start": v(-31.35, 124.9) * mm, "mid": v(-28.41, 123.43) * mm, "end": v(-25.42, 124.8) * mm});
            skLineSegment(sketch, "E328", {"start": v(-41.65, -73.44) * mm, "end": v(-31.12, -59.25) * mm});
            skLineSegment(sketch, "E329", {"start": v(-25.14, -59.07) * mm, "end": v(-18.76, -66.67) * mm});
            skLineSegment(sketch, "E330", {"start": v(-19.78, -72.42) * mm, "end": v(-34.89, -81.15) * mm});
            skPoint(sketch, "E331.visualSharp", {"position": v(-37.66, -82.75) * mm});
            skPoint(sketch, "E332.visualSharp", {"position": v(-43.44, -75.86) * mm});
            skArc(sketch, "E333.filletArc", {"start": v(-25.14, -59.07) * mm, "mid": v(-28.18, -57.7) * mm, "end": v(-31.12, -59.25) * mm});
            skArc(sketch, "E334.filletArc", {"start": v(-19.78, -72.42) * mm, "mid": v(-17.93, -69.78) * mm, "end": v(-18.76, -66.67) * mm});
            skLineSegment(sketch, "E335", {"start": v(215.98, -81.18) * mm, "end": v(200.17, -73.28) * mm});
            skLineSegment(sketch, "E336", {"start": v(198.96, -67.43) * mm, "end": v(205.34, -59.82) * mm});
            skLineSegment(sketch, "E337", {"start": v(211.17, -59.82) * mm, "end": v(222.4, -73.19) * mm});
            skPoint(sketch, "E338.visualSharp", {"position": v(224.45, -75.64) * mm});
            skPoint(sketch, "E339.visualSharp", {"position": v(218.67, -82.53) * mm});
            skArc(sketch, "E340.filletArc", {"start": v(198.96, -67.43) * mm, "mid": v(198.14, -70.65) * mm, "end": v(200.17, -73.28) * mm});
            skArc(sketch, "E341.filletArc", {"start": v(211.17, -59.82) * mm, "mid": v(208.26, -58.46) * mm, "end": v(205.34, -59.82) * mm});
            skArc(sketch, "E342", {"start": v(-66.15, 99.78) * mm, "mid": v(-71.7, 96.24) * mm, "end": v(-69.4, 90.07) * mm});
            skArc(sketch, "E343", {"start": v(-53.37, 123.14) * mm, "mid": v(-59.51, 120.78) * mm, "end": v(-58.48, 114.27) * mm});
            skArc(sketch, "E344", {"start": v(-35.33, 146.4) * mm, "mid": v(-41.8, 145.16) * mm, "end": v(-41.94, 138.57) * mm});
            skArc(sketch, "E345", {"start": v(-13.44, 167.4) * mm, "mid": v(-20.02, 167.4) * mm, "end": v(-21.43, 160.98) * mm});
            skArc(sketch, "E346", {"start": v(9.38, 182.48) * mm, "mid": v(2.9, 183.64) * mm, "end": v(0.4, 177.55) * mm});
            skArc(sketch, "E347", {"start": v(33.31, 192.78) * mm, "mid": v(27.14, 195.08) * mm, "end": v(23.6, 189.53) * mm});
            skArc(sketch, "E348", {"start": v(-74.04, 75.96) * mm, "mid": v(-79.11, 71.76) * mm, "end": v(-76.08, 65.92) * mm});
            skArc(sketch, "E349", {"start": v(-78.98, 50.92) * mm, "mid": v(-83.44, 46.07) * mm, "end": v(-79.65, 40.7) * mm});
            skArc(sketch, "E350", {"start": v(57.47, 199.46) * mm, "mid": v(51.62, 202.5) * mm, "end": v(47.42, 197.43) * mm});
            skArc(sketch, "E351", {"start": v(82.69, 203.03) * mm, "mid": v(77.3, 206.82) * mm, "end": v(72.47, 202.36) * mm});
            skArc(sketch, "E352.MirrorCS", {"start": v(98.12, 203.03) * mm, "mid": v(103.5, 206.82) * mm, "end": v(108.35, 202.36) * mm});
            skArc(sketch, "E353.MirrorCS", {"start": v(123.35, 199.46) * mm, "mid": v(129.19, 202.5) * mm, "end": v(133.39, 197.43) * mm});
            skArc(sketch, "E354.MirrorCS", {"start": v(147.5, 192.78) * mm, "mid": v(153.67, 195.08) * mm, "end": v(157.21, 189.53) * mm});
            skArc(sketch, "E355.MirrorCS", {"start": v(171.43, 182.48) * mm, "mid": v(177.91, 183.64) * mm, "end": v(180.42, 177.55) * mm});
            skArc(sketch, "E356.MirrorCS", {"start": v(194.25, 167.4) * mm, "mid": v(200.83, 167.4) * mm, "end": v(202.24, 160.98) * mm});
            skArc(sketch, "E357.MirrorCS", {"start": v(246.96, 99.78) * mm, "mid": v(252.5, 96.24) * mm, "end": v(250.21, 90.07) * mm});
            skArc(sketch, "E358.MirrorCS", {"start": v(254.86, 75.96) * mm, "mid": v(259.93, 71.76) * mm, "end": v(256.9, 65.92) * mm});
            skArc(sketch, "E359.MirrorCS", {"start": v(259.8, 50.92) * mm, "mid": v(264.25, 46.07) * mm, "end": v(260.46, 40.7) * mm});
            skArc(sketch, "E360", {"start": v(221.78, 139.03) * mm, "mid": v(221.61, 145.63) * mm, "end": v(215.11, 146.8) * mm});
            skArc(sketch, "E361", {"start": v(239.91, 114) * mm, "mid": v(241.07, 120.48) * mm, "end": v(234.98, 122.99) * mm});
            skArc(sketch, "E362.MirrorCS", {"start": v(-78.98, 15.04) * mm, "mid": v(-83.44, 19.88) * mm, "end": v(-79.65, 25.26) * mm});
            skArc(sketch, "E363.MirrorCS", {"start": v(-74.04, -10) * mm, "mid": v(-79.11, -5.8) * mm, "end": v(-76.08, 0.04) * mm});
            skArc(sketch, "E364.MirrorCS", {"start": v(-66.15, -33.83) * mm, "mid": v(-71.7, -30.29) * mm, "end": v(-69.4, -24.12) * mm});
            skArc(sketch, "E365.MirrorCS", {"start": v(-13.44, -101.44) * mm, "mid": v(-20.02, -101.46) * mm, "end": v(-21.43, -95.03) * mm});
            skArc(sketch, "E366.MirrorCS", {"start": v(9.38, -116.53) * mm, "mid": v(2.9, -117.69) * mm, "end": v(0.4, -111.6) * mm});
            skArc(sketch, "E367.MirrorCS", {"start": v(33.31, -126.83) * mm, "mid": v(27.14, -129.13) * mm, "end": v(23.6, -123.58) * mm});
            skArc(sketch, "E368.MirrorCS", {"start": v(57.47, -133.51) * mm, "mid": v(51.62, -136.54) * mm, "end": v(47.42, -131.47) * mm});
            skArc(sketch, "E369.MirrorCS", {"start": v(82.69, -137.08) * mm, "mid": v(77.3, -140.87) * mm, "end": v(72.47, -136.41) * mm});
            skArc(sketch, "E370.MirrorCS", {"start": v(98.12, -137.08) * mm, "mid": v(103.5, -140.87) * mm, "end": v(108.35, -136.41) * mm});
            skArc(sketch, "E371.MirrorCS", {"start": v(123.35, -133.51) * mm, "mid": v(129.19, -136.54) * mm, "end": v(133.39, -131.47) * mm});
            skArc(sketch, "E372.MirrorCS", {"start": v(147.5, -126.83) * mm, "mid": v(153.67, -129.13) * mm, "end": v(157.21, -123.58) * mm});
            skArc(sketch, "E373.MirrorCS", {"start": v(171.43, -116.53) * mm, "mid": v(177.91, -117.69) * mm, "end": v(180.42, -111.6) * mm});
            skArc(sketch, "E374.MirrorCS", {"start": v(194.25, -101.44) * mm, "mid": v(200.83, -101.46) * mm, "end": v(202.24, -95.03) * mm});
            skArc(sketch, "E375.MirrorCS", {"start": v(239.91, -48.05) * mm, "mid": v(241.07, -54.53) * mm, "end": v(234.98, -57.04) * mm});
            skArc(sketch, "E376.MirrorCS", {"start": v(246.96, -33.83) * mm, "mid": v(252.5, -30.29) * mm, "end": v(250.21, -24.12) * mm});
            skArc(sketch, "E377.MirrorCS", {"start": v(254.86, -10) * mm, "mid": v(259.93, -5.8) * mm, "end": v(256.9, 0.04) * mm});
            skArc(sketch, "E378.MirrorCS", {"start": v(259.8, 15.04) * mm, "mid": v(264.25, 19.88) * mm, "end": v(260.46, 25.26) * mm});
            skArc(sketch, "E379", {"start": v(-59.1, -48.05) * mm, "mid": v(-60.32, -54.57) * mm, "end": v(-54.17, -57.04) * mm});
            skArc(sketch, "E380", {"start": v(-41.65, -73.44) * mm, "mid": v(-41.43, -80.07) * mm, "end": v(-34.89, -81.15) * mm});
            skArc(sketch, "E381", {"start": v(215.98, -81.18) * mm, "mid": v(222.41, -79.77) * mm, "end": v(222.4, -73.19) * mm});
            skArc(sketch, "E382", {"start": v(-246.24, 67.65) * mm, "mid": v(-248.73, 73.75) * mm, "end": v(-255.21, 72.6) * mm});
            skArc(sketch, "E383", {"start": v(-223.3, 48.48) * mm, "mid": v(-223.54, 55.1) * mm, "end": v(-230.08, 56.15) * mm});
            skArc(sketch, "E384", {"start": v(-208.87, 24.89) * mm, "mid": v(-207.44, 31.31) * mm, "end": v(-213.41, 34.07) * mm});
            skArc(sketch, "E385", {"start": v(-202.55, -2.72) * mm, "mid": v(-199.17, 2.99) * mm, "end": v(-204.1, 7.41) * mm});
            skArc(sketch, "E386", {"start": v(-276.67, 77.95) * mm, "mid": v(-281.3, 82.7) * mm, "end": v(-286.86, 79.07) * mm});
            skArc(sketch, "E387", {"start": v(-302.17, 79.14) * mm, "mid": v(-307.67, 82.77) * mm, "end": v(-312.37, 78.14) * mm});
            skArc(sketch, "E388", {"start": v(-333.8, 72.69) * mm, "mid": v(-340.27, 73.92) * mm, "end": v(-342.82, 67.84) * mm});
            skArc(sketch, "E389", {"start": v(-358.91, 56.25) * mm, "mid": v(-365.45, 55.26) * mm, "end": v(-365.8, 48.66) * mm});
            skArc(sketch, "E390", {"start": v(-375.59, 34.19) * mm, "mid": v(-381.63, 31.5) * mm, "end": v(-380.22, 25.05) * mm});
            skArc(sketch, "E391", {"start": v(-384.91, 7.54) * mm, "mid": v(-389.85, 3.15) * mm, "end": v(-386.54, -2.57) * mm});
            skArc(sketch, "E392", {"start": v(-386.75, -20.98) * mm, "mid": v(-390.06, -26.67) * mm, "end": v(-385.2, -31.1) * mm});
            skArc(sketch, "E393", {"start": v(-380.43, -48.58) * mm, "mid": v(-381.86, -55) * mm, "end": v(-375.89, -57.77) * mm});
            skArc(sketch, "E394", {"start": v(-366, -72.18) * mm, "mid": v(-365.7, -78.75) * mm, "end": v(-359.22, -79.85) * mm});
            skArc(sketch, "E395", {"start": v(-343.06, -91.35) * mm, "mid": v(-340.57, -97.44) * mm, "end": v(-334.09, -96.3) * mm});
            skArc(sketch, "E396", {"start": v(-312.63, -101.65) * mm, "mid": v(-308, -106.39) * mm, "end": v(-302.44, -102.77) * mm});
            skArc(sketch, "E397", {"start": v(-286.86, -102.77) * mm, "mid": v(-281.31, -106.32) * mm, "end": v(-276.67, -101.65) * mm});
            skArc(sketch, "E398", {"start": v(-255.21, -96.3) * mm, "mid": v(-248.7, -97.5) * mm, "end": v(-246.24, -91.35) * mm});
            skArc(sketch, "E399", {"start": v(-230.08, -79.85) * mm, "mid": v(-223.6, -78.75) * mm, "end": v(-223.3, -72.18) * mm});
            skArc(sketch, "E400", {"start": v(-213.41, -57.77) * mm, "mid": v(-207.37, -55.04) * mm, "end": v(-208.87, -48.58) * mm});
            skArc(sketch, "E401", {"start": v(-204.1, -31.1) * mm, "mid": v(-199.17, -26.68) * mm, "end": v(-202.55, -20.98) * mm});
            skSolve(sketch);
        }
        {
            var Q0;
            Q0=qSketchRegion(id+"F0",true);
            extrude(context, id + "F1", {"entities" : qUnion([Q0]), "depth" : 25.4 * mm});
        }
    });
